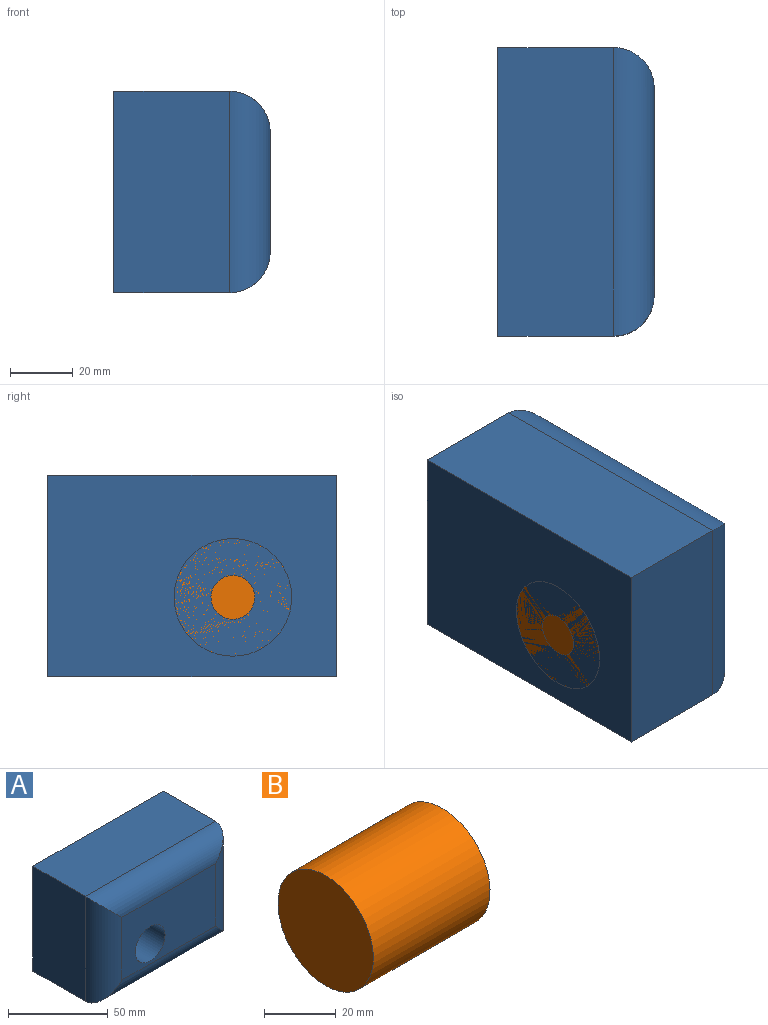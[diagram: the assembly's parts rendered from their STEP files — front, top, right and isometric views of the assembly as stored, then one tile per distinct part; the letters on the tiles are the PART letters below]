
ASSEMBLY  parts=2 mates=1
PART A: 13 faces, bbox 92.3x50x64.3 mm
  f0: plane 92.26x37mm, normal (0,0,1), area 3413.7mm2, adj f1,f3,f5,f6
  f1: plane 64.34x37mm, normal (-1,0,0), area 2380.6mm2, adj f0,f2,f5,f7
  f2: plane 92.26x37mm, normal (0,0,-1), area 3413.7mm2, adj f1,f3,f5,f9
  f3: plane 64.34x37mm, normal (1,0,0), area 2380.6mm2, adj f0,f2,f5,f8
  f4: plane 66.26x38.34mm, normal (0,-1,0), area 2194.1mm2, adj f6,f7,f8,f9,f12
  f5: plane 92.26x64.34mm, normal (0,1,0), area 5782.2mm2, adj f0,f1,f2,f3,f10
  f6: cylinder r=13mm len=92.26mm, axis (1,0,0), area 1691.1mm2, adj f0,f4,f7,f8
  f7: cylinder r=13mm len=64.34mm, axis (0,0,1), area 1120.9mm2, adj f1,f4,f6,f9
  f8: cylinder r=13mm len=64.34mm, axis (0,0,-1), area 1120.9mm2, adj f3,f4,f6,f9
  f9: cylinder r=13mm len=92.26mm, axis (-1,0,0), area 1691.1mm2, adj f2,f4,f7,f8
  f10: cylinder r=7mm len=32.2mm, axis (0,-1,0), area 1416.2mm2, adj f5,f11
  f11: plane 21x21mm, normal (0,-1,0), area 192.4mm2, adj f10,f12
  f12: cylinder r=10.5mm len=21mm, axis (0,-1,0), area 1174.3mm2, adj f4,f11
PART B: 3 faces, bbox 46x37.6x37.6 mm
  f0: cylinder r=18.81mm len=46mm, axis (-1,0,0), area 5437.4mm2, adj f1,f2
  f1: plane 37.63x37.63mm, normal (1,0,0), area 1111.9mm2, adj f0
  f2: plane 37.63x37.63mm, normal (-1,0,0), area 1111.9mm2, adj f0
PLACE A rot(axis=(0,0,1),90deg) t=(-16.95,-134.3,-20.78)mm
PLACE B t=(-16.95,41.72,0.66)mm
MATE revolute A.f10 <-> B.f0  axis (1,0,0) through (33.05,-101.24,-14.55)mm
